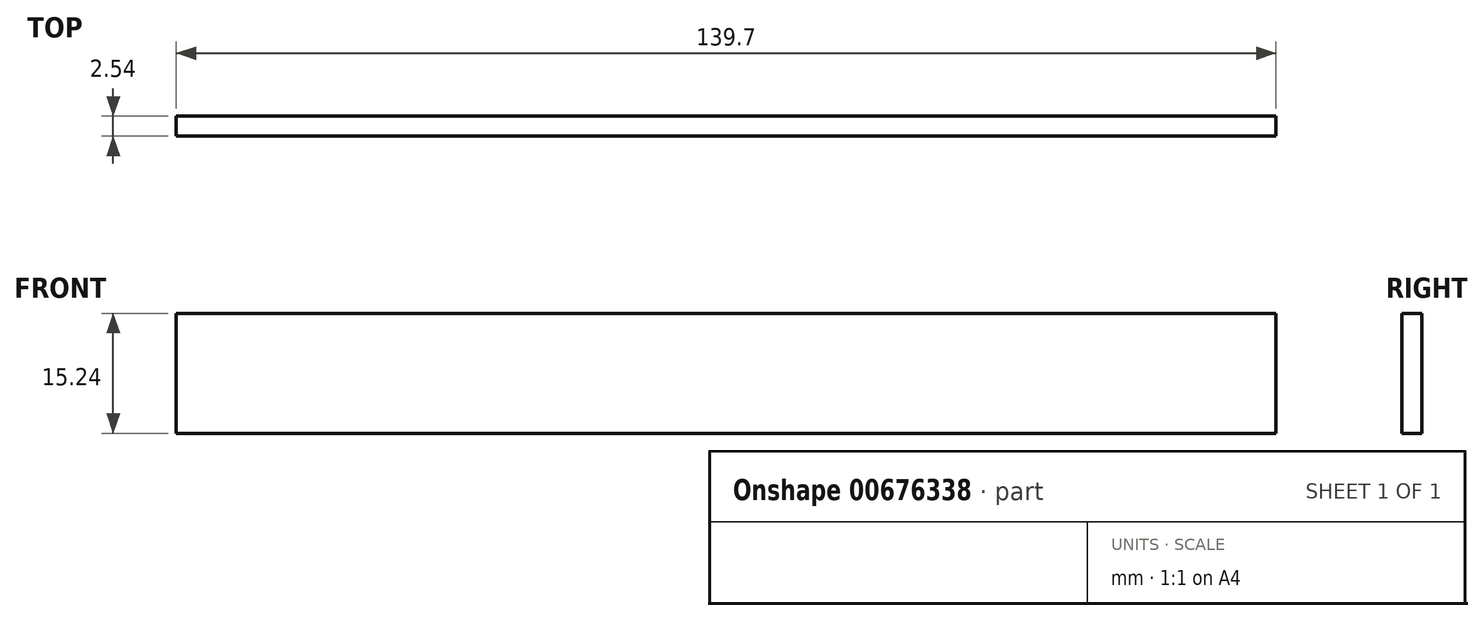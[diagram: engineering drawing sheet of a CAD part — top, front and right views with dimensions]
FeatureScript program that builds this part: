
annotation { "Feature Type Name" : "Feature", "Feature Type Description" : "" }
export const myFeature = defineFeature(function(context is Context, id is Id, definition is map)
    precondition{}
    {
        {
            var Q0;
            Q0=qCreatedBy(makeId("Front.planeOp"),FACE);
            var sketch = newSketch(context, id + "F0", { "sketchPlane" : qUnion([Q0])});
            skLineSegment(sketch, "E0", {"start": v(0, 0) * mm, "end": v(-139.7, 0) * mm});
            skLineSegment(sketch, "E1", {"start": v(-139.7, 0) * mm, "end": v(-139.7, 15.24) * mm});
            skLineSegment(sketch, "E2", {"start": v(-139.7, 15.24) * mm, "end": v(0, 15.24) * mm});
            skLineSegment(sketch, "E3", {"start": v(0, 15.24) * mm, "end": v(0, 0) * mm});
            skSolve(sketch);
        }
        {
            var Q0;
            Q0 = qSketchRegion(id + "F0", true);
            extrude(context, id + "F1", {"entities" : qUnion([Q0]), "depth" : 2.54 * mm, "offsetDistance" : 25.4 * mm});
        }
    });
